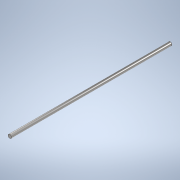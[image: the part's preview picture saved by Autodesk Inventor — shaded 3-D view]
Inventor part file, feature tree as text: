
AUTODESK INVENTOR PART (.ipt)
format: ipt  version: 2022 (Build 260153070, 153G)  size: 94,720 bytes
history: native  units: mm
features: extrude x1, sketch x1
ambient origin geometry x8: Origin, YZ Plane, XZ Plane, XY Plane, X Axis, Y Axis, Z Axis, Center Point
bodies: Solid1 (feature_tree)
feature tree (2):
  extrude  "Extrusion1"  Depth=680.0mm TaperAngle=0.0deg
  sketch  "Sketch1"  dims[d0=15.24mm d1=680.0mm d2=0.0mm]
